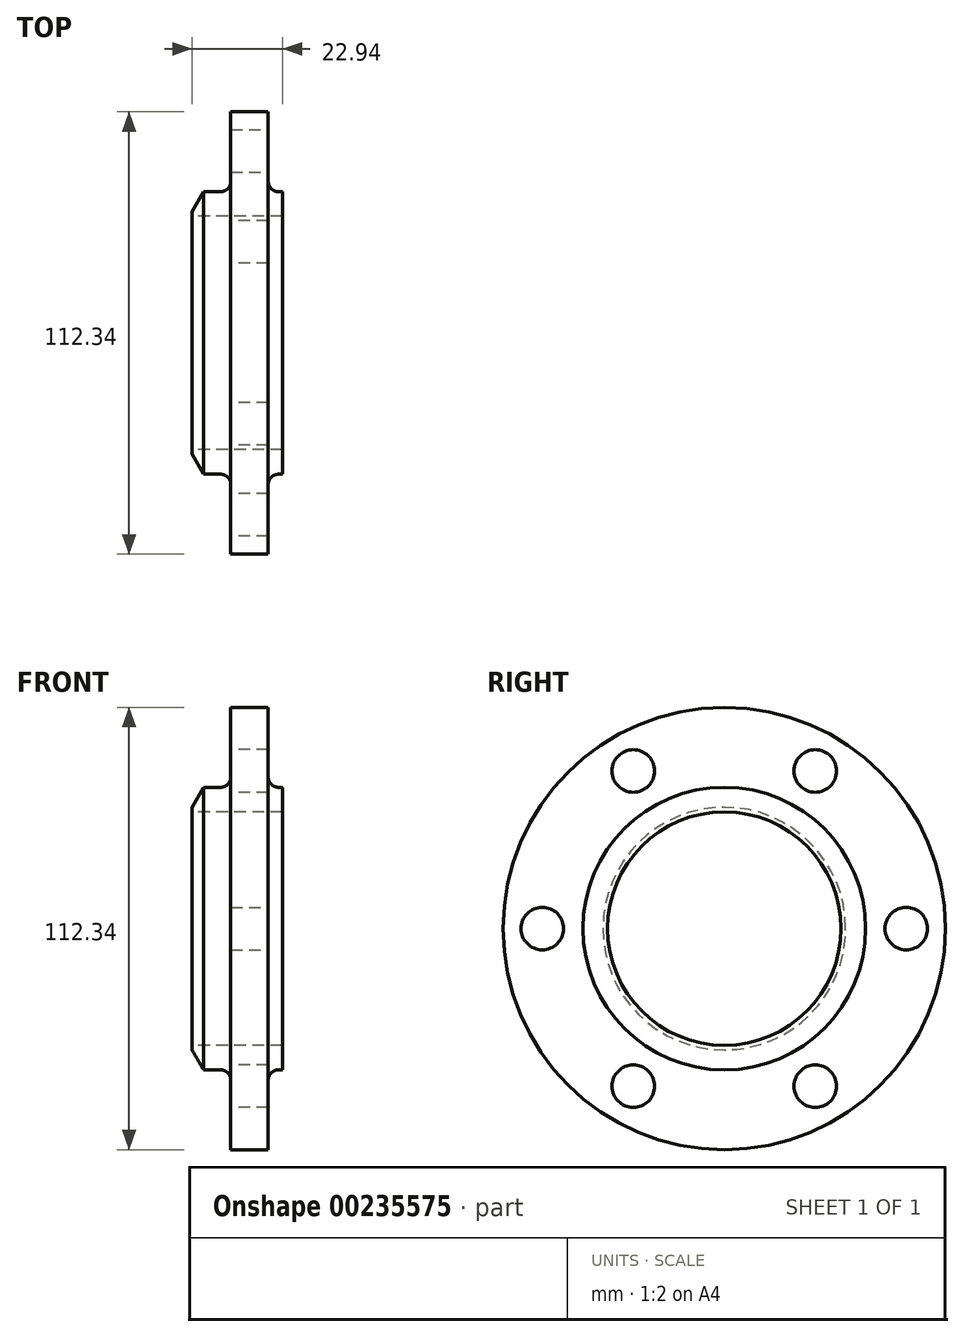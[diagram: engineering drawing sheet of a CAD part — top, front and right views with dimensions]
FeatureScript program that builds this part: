
annotation { "Feature Type Name" : "Feature", "Feature Type Description" : "" }
export const myFeature = defineFeature(function(context is Context, id is Id, definition is map)
    precondition{}
    {
        {
            var Q0;
            Q0=qCreatedBy(makeId("Top.planeOp"),FACE);
            var sketch = newSketch(context, id + "F0", { "sketchPlane" : qUnion([Q0])});
            skLineSegment(sketch, "E0", {"start": v(-76.14, 0) * mm, "end": v(76.73, 0) * mm, "construction": true});
            skSolve(sketch);
        }
        {
            var Q0;
            Q0=qCreatedBy(makeId("Top.planeOp"),FACE);
            var sketch = newSketch(context, id + "F1", { "sketchPlane" : qUnion([Q0])});
            skLineSegment(sketch, "E1.bottom", {"start": v(40.08, 56.17) * mm, "end": v(49.62, 56.17) * mm});
            skLineSegment(sketch, "E1.top", {"start": v(40.08, 35.9) * mm, "end": v(49.62, 35.9) * mm});
            skLineSegment(sketch, "E1.left", {"start": v(40.08, 56.17) * mm, "end": v(40.08, 35.9) * mm});
            skLineSegment(sketch, "E1.right", {"start": v(49.62, 56.17) * mm, "end": v(49.62, 35.9) * mm});
            skPoint(sketch, "E2.firstSnap0", {"position": v(44.85, 35.9) * mm});
            skLineSegment(sketch, "E2.bottom", {"start": v(30.25, 35.9) * mm, "end": v(53.2, 35.9) * mm});
            skLineSegment(sketch, "E2.top", {"start": v(30.25, 29.65) * mm, "end": v(53.2, 29.65) * mm});
            skLineSegment(sketch, "E2.left", {"start": v(30.25, 35.9) * mm, "end": v(30.25, 29.65) * mm});
            skLineSegment(sketch, "E2.right", {"start": v(53.2, 35.9) * mm, "end": v(53.2, 29.65) * mm});
            skSolve(sketch);
        }
        {
            var Q0;
            Q0=makeQuery(id+"F1.imprint","IMPRINT",FACE,{"disambiguationData":[TD([[makeQuery(id+"F1.imprint","IMPRINT",EDGE,{"derivedFrom":sQuery(id+"F1.wireOp",EDGE,"E1.bottom")}),-1.0]])]});
            var Q1;
            Q1=makeQuery(id+"F1.imprint","IMPRINT",FACE,{"disambiguationData":[TD([[makeQuery(id+"F1.imprint","IMPRINT",EDGE,{"derivedFrom":sQuery(id+"F1.wireOp",EDGE,"E2.top")}),1.0]])]});
            var Q2;
            Q2=sQuery(id+"F0.wireOp",EDGE,"E0");
            revolve(context, id + "F2", {"entities" : qUnion([Q0, Q1]), "axis" : qUnion([Q2]), "revolveType" : RevolveType.FULL});
        }
        {
            var Q0;
            Q0=makeQuery(id+"F2.opRevolve","SWEPT_EDGE",EDGE,{"disambiguationData":[OSD([sQuery(id+"F1.wireOp",EDGE,"E1.right"),sQuery(id+"F1.wireOp",EDGE,"E2.bottom")])]});
            fillet(context, id + "F3", {"entities" : qUnion([Q0]), "radius" : 2.54 * mm, "tangentPropagation" : true, "allowEdgeOverflow" : false});
        }
        {
            var Q0;
            Q0=makeQuery(id+"F2.opRevolve","SWEPT_EDGE",EDGE,{"disambiguationData":[OSD([sQuery(id+"F1.wireOp",EDGE,"E1.left"),sQuery(id+"F1.wireOp",EDGE,"E2.bottom")])]});
            fillet(context, id + "F4", {"entities" : qUnion([Q0]), "radius" : 2.54 * mm, "tangentPropagation" : true, "allowEdgeOverflow" : false});
        }
        {
            var Q0;
            Q0=makeQuery(id+"F2.opRevolve","SWEPT_EDGE",EDGE,{"disambiguationData":[OSD([sQuery(id+"F1.wireOp",EDGE,"E2.bottom"),sQuery(id+"F1.wireOp",EDGE,"E2.left")])]});
            chamfer(context, id + "F5", {"entities" : qUnion([Q0]), "chamferType" : ChamferType.OFFSET_ANGLE, "width" : 5.08 * mm, "oppositeDirection" : false, "angle" : 30 * degree, "tangentPropagation" : true});
        }
        {
            var Q0;
            Q0=makeQuery(id+"F2.opRevolve","SWEPT_FACE",FACE,{"disambiguationData":[OSD([sQuery(id+"F1.wireOp",EDGE,"E1.left")])]});
            var sketch = newSketch(context, id + "F6", { "sketchPlane" : qUnion([Q0])});
            skCircle(sketch, "E3", {"center": v(0, 0) * mm, "radius": 46.24 * mm, "construction": true});
            skLineSegment(sketch, "E4", {"start": v(-76.11, 0) * mm, "end": v(75.23, 0) * mm, "construction": true});
            skCircle(sketch, "E5", {"center": v(-46.24, 0) * mm, "radius": 5.4 * mm});
            skCircle(sketch, "E6.1.0", {"center": v(-23.12, -40.05) * mm, "radius": 5.4 * mm});
            skCircle(sketch, "E6.2.0", {"center": v(23.12, -40.05) * mm, "radius": 5.4 * mm});
            skCircle(sketch, "E6.3.0", {"center": v(46.24, 0) * mm, "radius": 5.4 * mm});
            skCircle(sketch, "E6.4.0", {"center": v(23.12, 40.05) * mm, "radius": 5.4 * mm});
            skCircle(sketch, "E6.5.0", {"center": v(-23.12, 40.05) * mm, "radius": 5.4 * mm});
            skSolve(sketch);
        }
        {
            var Q0;
            Q0=makeQuery(id+"F6.imprint","IMPRINT",FACE,{"disambiguationData":[TD([[makeQuery(id+"F6.imprint","IMPRINT",EDGE,{"derivedFrom":sQuery(id+"F6.wireOp",EDGE,"E5")}),1.0]])]});
            extrude(context, id + "F7", {"entities" : qUnion([Q0]), "operationType" : NewBodyOperationType.REMOVE, "depth" : 25.4 * mm, "hasSecondDirection" : true, "secondDirectionOppositeDirection" : true, "secondDirectionDepth" : 25.4 * mm});
        }
        {
            var Q0;
            Q0 = qSketchRegion(id + "F6", true);
            extrude(context, id + "F8", {"entities" : qUnion([Q0]), "operationType" : NewBodyOperationType.REMOVE, "oppositeDirection" : true, "depth" : 25.4 * mm, "hasSecondDirection" : true, "secondDirectionOppositeDirection" : false, "secondDirectionDepth" : 25.4 * mm});
        }
    });
